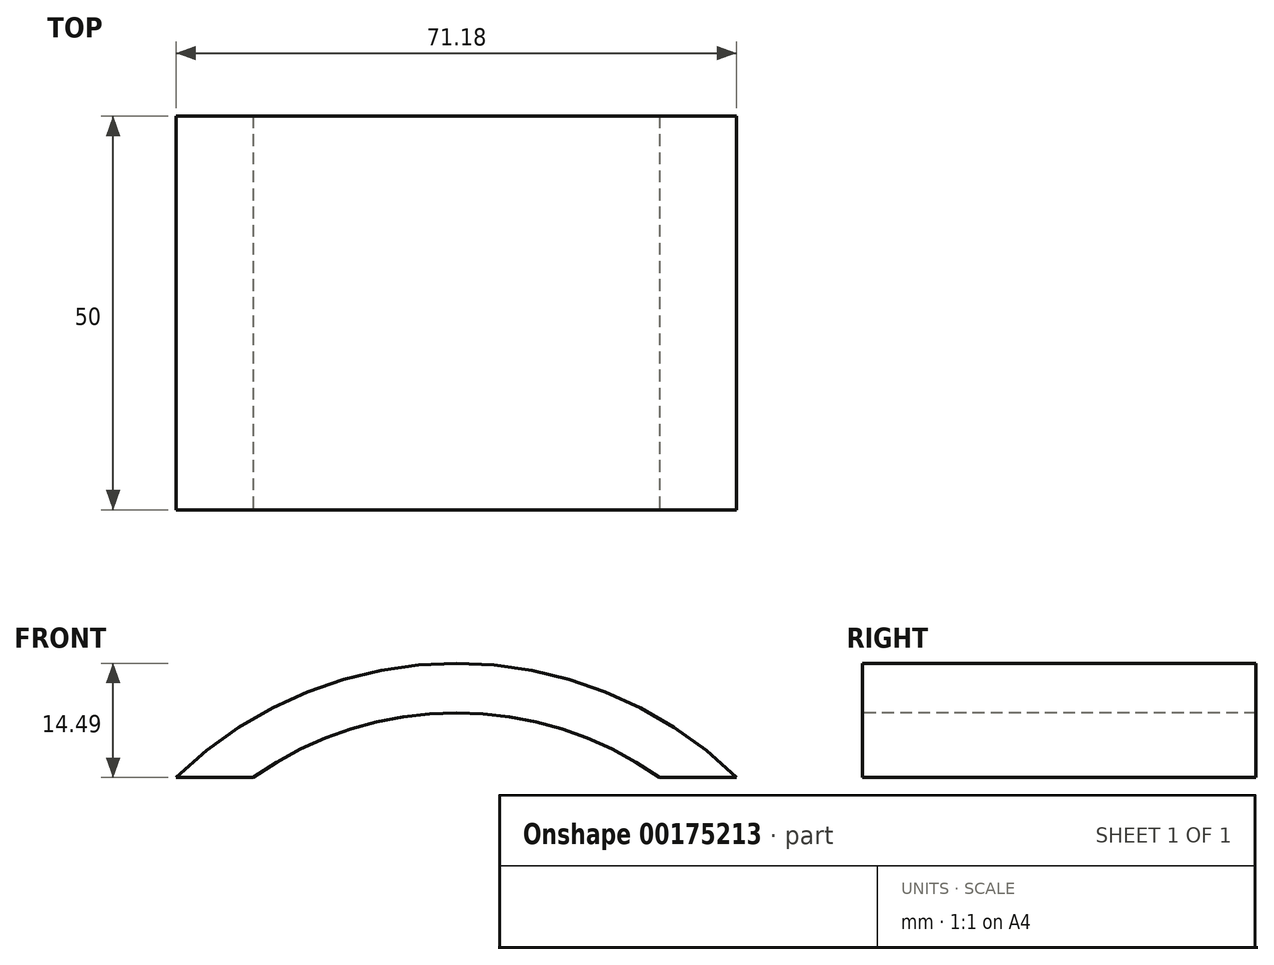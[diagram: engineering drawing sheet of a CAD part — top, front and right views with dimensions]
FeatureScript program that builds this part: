
annotation { "Feature Type Name" : "Feature", "Feature Type Description" : "" }
export const myFeature = defineFeature(function(context is Context, id is Id, definition is map)
    precondition{}
    {
        {
            var Q0;
            Q0=qCreatedBy(makeId("Front.planeOp"),FACE);
            var sketch = newSketch(context, id + "F0", { "sketchPlane" : qUnion([Q0])});
            skArc(sketch, "E0", {"start": v(5.13, 23.53) * mm, "mid": v(-20.68, 31.74) * mm, "end": v(-46.5, 23.53) * mm});
            skArc(sketch, "E1", {"start": v(14.91, 23.53) * mm, "mid": v(-20.68, 38.02) * mm, "end": v(-56.27, 23.53) * mm});
            skLineSegment(sketch, "E2", {"start": v(-46.5, 23.53) * mm, "end": v(-56.27, 23.53) * mm});
            skLineSegment(sketch, "E3", {"start": v(5.13, 23.53) * mm, "end": v(14.91, 23.53) * mm});
            skSolve(sketch);
        }
        {
            var Q0;
            Q0=makeQuery(id+"F0.imprint","IMPRINT",FACE,{"disambiguationData":[TD([[makeQuery(id+"F0.imprint","IMPRINT",EDGE,{"derivedFrom":sQuery(id+"F0.wireOp",EDGE,"E0")}),-1.0]])]});
            var Q1;
            Q1 = qConstructionFilter(qBodyType(qCreatedBy(id + "F0" ,EDGE), BodyType.WIRE), ConstructionObject.NO);
            extrude(context, id + "F1", {"entities" : qUnion([Q0]), "surfaceEntities" : qUnion([Q1]), "oppositeDirection" : true, "depth" : 50 * mm});
        }
    });
